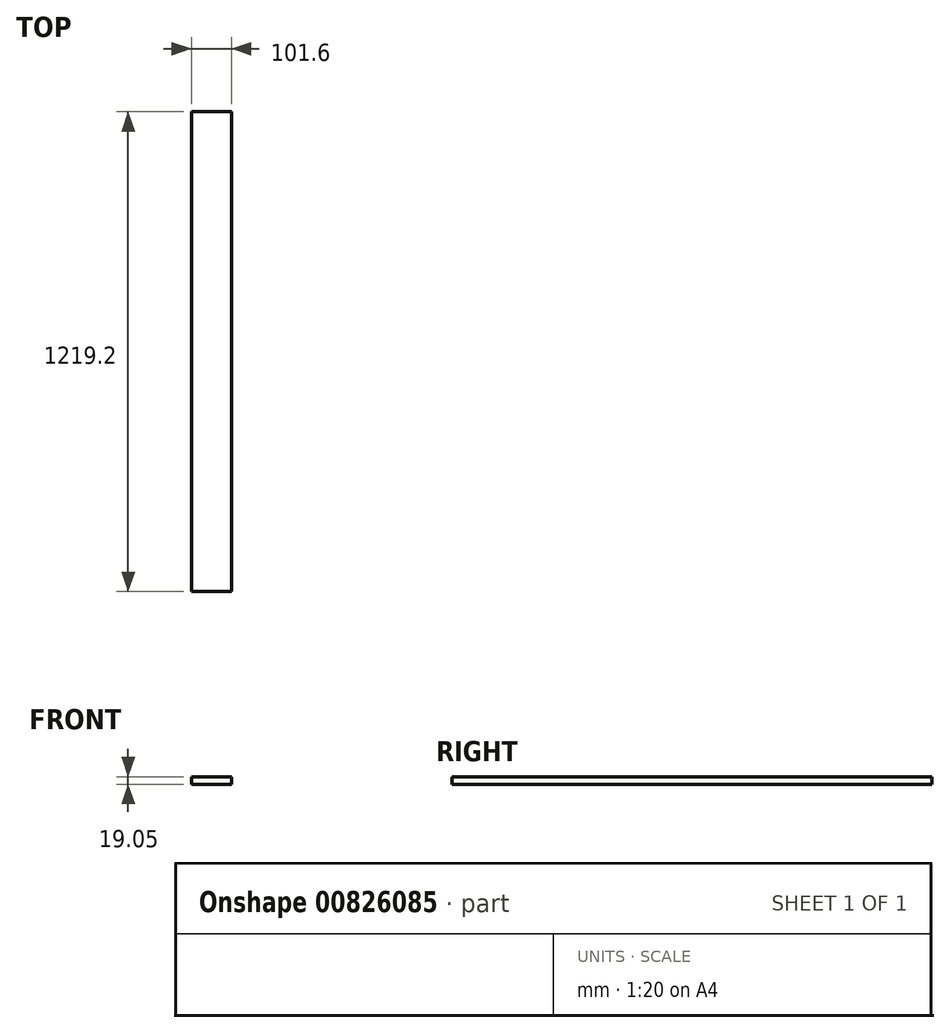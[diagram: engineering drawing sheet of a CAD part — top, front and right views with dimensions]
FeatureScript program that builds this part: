
annotation { "Feature Type Name" : "Feature", "Feature Type Description" : "" }
export const myFeature = defineFeature(function(context is Context, id is Id, definition is map)
    precondition{}
    {
        {
            var Q0;
            Q0=qCreatedBy(makeId("Front.planeOp"),FACE);
            var sketch = newSketch(context, id + "F0", { "sketchPlane" : qUnion([Q0])});
            skLineSegment(sketch, "E0.bottom", {"start": v(0, 0) * mm, "end": v(-101.6, 0) * mm});
            skLineSegment(sketch, "E0.top", {"start": v(0, 19.05) * mm, "end": v(-101.6, 19.05) * mm});
            skLineSegment(sketch, "E0.left", {"start": v(0, 0) * mm, "end": v(0, 19.05) * mm});
            skLineSegment(sketch, "E0.right", {"start": v(-101.6, 0) * mm, "end": v(-101.6, 19.05) * mm});
            skSolve(sketch);
        }
        {
            var Q0;
            Q0 = qSketchRegion(id + "F0", true);
            extrude(context, id + "F1", {"entities" : qUnion([Q0]), "depth" : 1219.2 * mm, "offsetDistance" : 25 * mm});
        }
    });
